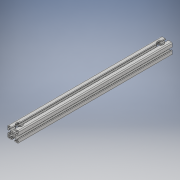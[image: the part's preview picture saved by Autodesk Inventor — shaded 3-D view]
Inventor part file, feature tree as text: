
AUTODESK INVENTOR PART (.ipt)
format: ipt  version: 2018 (Build 220112000, 112)  size: 561,664 bytes
history: native  units: in
note: dims shown in document units (in); Inventor stores cm internally (conversion verified against a paired STEP export)
features: move_body x3, direct_edit x1, extrude x1, sketch x1, other x1
ambient origin geometry x8: Origin, YZ Plane, XZ Plane, XY Plane, X Axis, Y Axis, Z Axis, Center Point
bodies: Solid1 (feature_tree)
feature tree (7):
  direct_edit  "Direct Edit1"
  extrude  "Extrusion1"  Depth=24.0in TaperAngle=0.0deg
  sketch  "Sketch1"  dims[d0=0.0in d1=0.0in d2=122.0472in d3=0.0in d4=0.0in d5=24.0in d6=0.0in d7=0.0in d8=21.0in d9=0.855in d10=0.813in d11=0.855in d12=0.813in d13=0.66in d14=0.0in]
  other  "8020-1515-LS-1515-LS X 145_1_1:1"
  move_body  "Move1"
  move_body  "Move2"
  move_body  "Move3"
